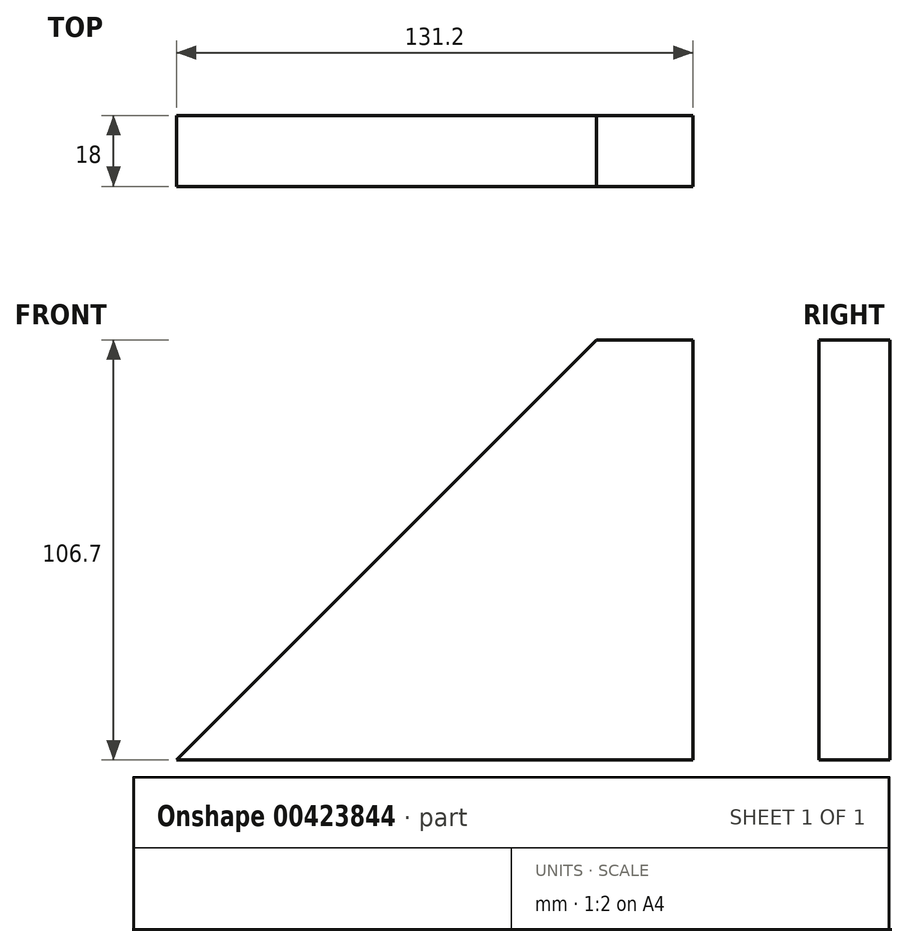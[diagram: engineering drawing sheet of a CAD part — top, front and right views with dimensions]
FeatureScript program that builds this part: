
annotation { "Feature Type Name" : "Feature", "Feature Type Description" : "" }
export const myFeature = defineFeature(function(context is Context, id is Id, definition is map)
    precondition{}
    {
        {
            var Q0;
            Q0=qCreatedBy(makeId("Front.planeOp"),FACE);
            var sketch = newSketch(context, id + "F0", { "sketchPlane" : qUnion([Q0])});
            skLineSegment(sketch, "E0", {"start": v(0, 0) * mm, "end": v(106.7, 106.7) * mm});
            skLineSegment(sketch, "E1", {"start": v(106.7, 106.7) * mm, "end": v(131.2, 106.7) * mm});
            skLineSegment(sketch, "E2", {"start": v(131.2, 106.7) * mm, "end": v(131.2, 0) * mm});
            skLineSegment(sketch, "E3", {"start": v(131.2, 0) * mm, "end": v(0, 0) * mm});
            skSolve(sketch);
        }
        {
            var Q0;
            Q0=qSketchRegion(id+"F0",true);
            extrude(context, id + "F1", {"entities" : qUnion([Q0]), "depth" : 18 * mm});
        }
    });
